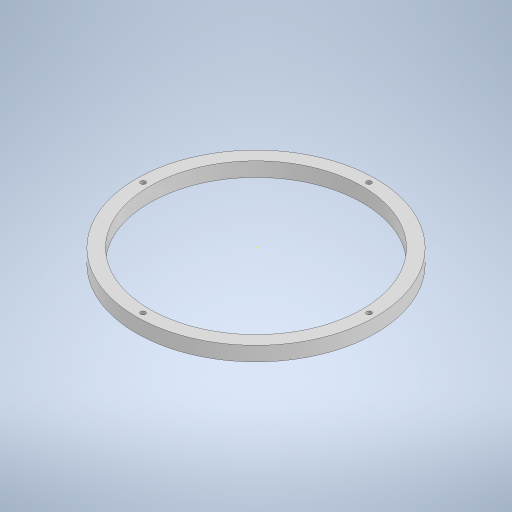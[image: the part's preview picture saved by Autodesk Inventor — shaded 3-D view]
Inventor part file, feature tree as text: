
AUTODESK INVENTOR PART (.ipt)
format: ipt  version: 2023 (Build 270158000, 158)  size: 256,000 bytes
history: native  units: in
note: dims shown in document units (in); Inventor stores cm internally (conversion verified against a paired STEP export)
features: sketch x3, extrude x1, hole x1, pattern_circular x1
ambient origin geometry x8: Origin, YZ Plane, XZ Plane, XY Plane, X Axis, Y Axis, Z Axis, Center Point
bodies: Solid1 (feature_tree)
feature tree (6):
  extrude  "Extrusion1"  Depth=8.7598in
  hole  "Hole1"  [1 undecoded]
  pattern_circular  "Circular Pattern1"  Count=4 Angle=360.0deg
  sketch  "Sketch3"  dims[d6=0.1969in d7=0.2362in d8=0.1969in d9=0.0787in d10=90.0deg d11=0.315in d12=0.8108in d13=1.5748in d14=360.0deg]
  sketch  "Sketch1"  dims[d0=9.8425in d1=8.7598in]
  sketch  "Sketch2"  dims[d2=0.5906in d3=0.0in d4=9.3012in]
note: 1 required parameter value undecoded (feature->parameter linkage not recoverable at this tier; creation-order binding heuristic only, values carry confidence <= 0.55)
